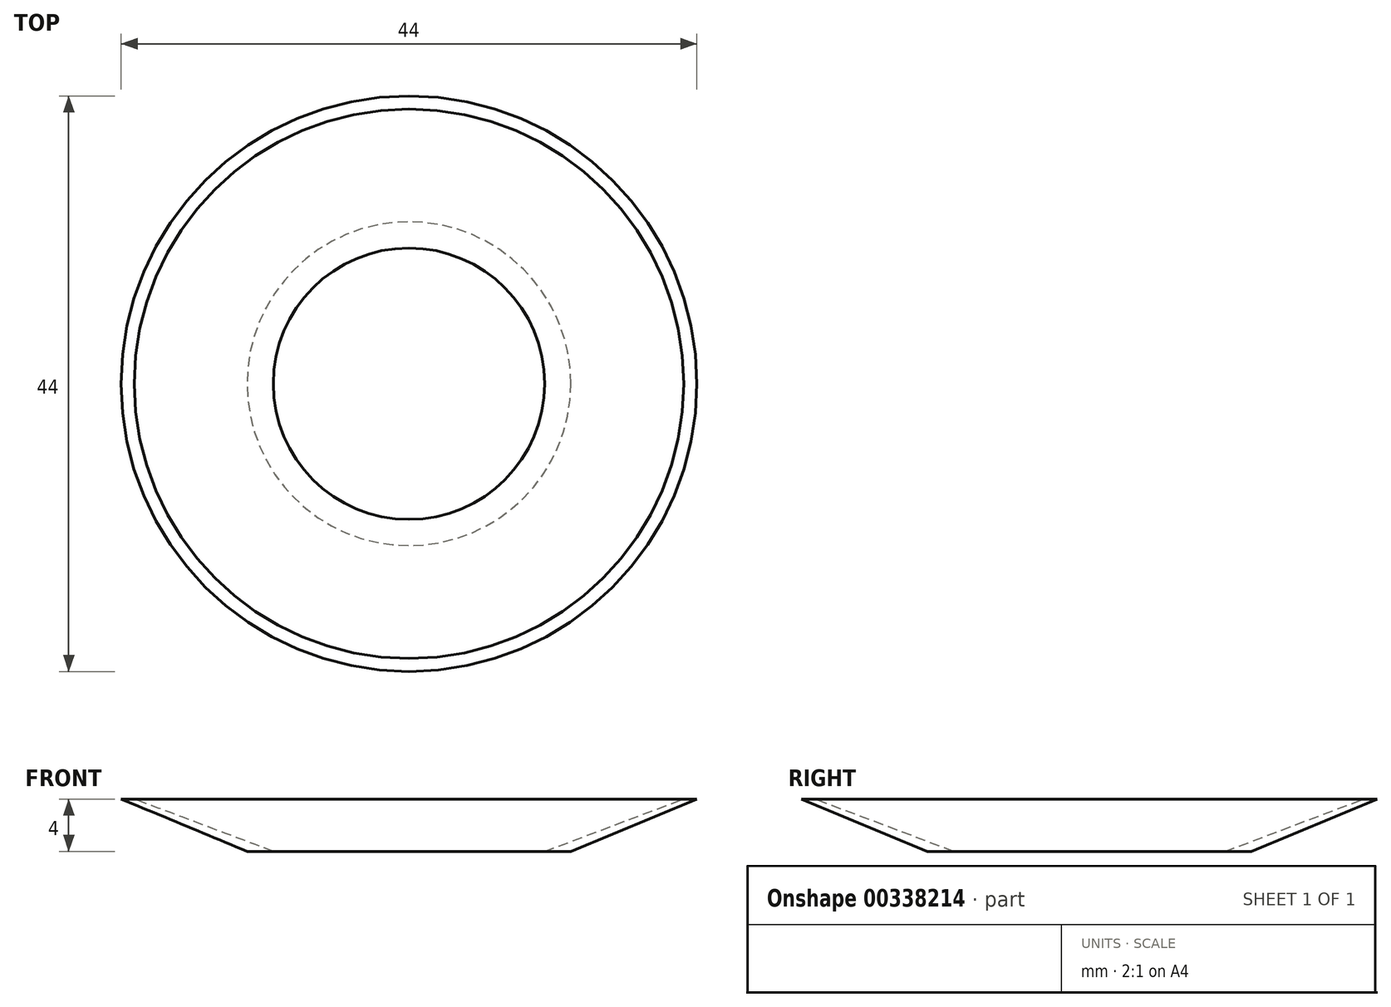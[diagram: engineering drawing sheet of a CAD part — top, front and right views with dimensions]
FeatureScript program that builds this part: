
annotation { "Feature Type Name" : "Feature", "Feature Type Description" : "" }
export const myFeature = defineFeature(function(context is Context, id is Id, definition is map)
    precondition{}
    {
        {
            var Q0;
            Q0=qCreatedBy(makeId("Front.planeOp"),FACE);
            var sketch = newSketch(context, id + "F0", { "sketchPlane" : qUnion([Q0])});
            skLineSegment(sketch, "E0", {"start": v(0, 0) * mm, "end": v(0, 4) * mm, "construction": true});
            skLineSegment(sketch, "E1", {"start": v(0, 4) * mm, "end": v(-22, 4) * mm, "construction": true});
            skLineSegment(sketch, "E2", {"start": v(-21, 4) * mm, "end": v(-22, 4) * mm});
            skLineSegment(sketch, "E3", {"start": v(-10.37, 0) * mm, "end": v(-12.38, 0) * mm, "construction": true});
            skLineSegment(sketch, "E4", {"start": v(-22, 4) * mm, "end": v(-12.37, 0) * mm});
            skLineSegment(sketch, "E5", {"start": v(-10.37, 0) * mm, "end": v(-21, 4) * mm});
            skLineSegment(sketch, "E6", {"start": v(-12.38, 0) * mm, "end": v(-10.37, 0) * mm});
            skSolve(sketch);
        }
        {
            var Q0;
            Q0 = qSketchRegion(id + "F0", true);
            var Q1;
            Q1=sQuery(id+"F0.wireOp",EDGE,"E0");
            revolve(context, id + "F1", {"entities" : qUnion([Q0]), "axis" : qUnion([Q1]), "revolveType" : RevolveType.FULL});
        }
    });
